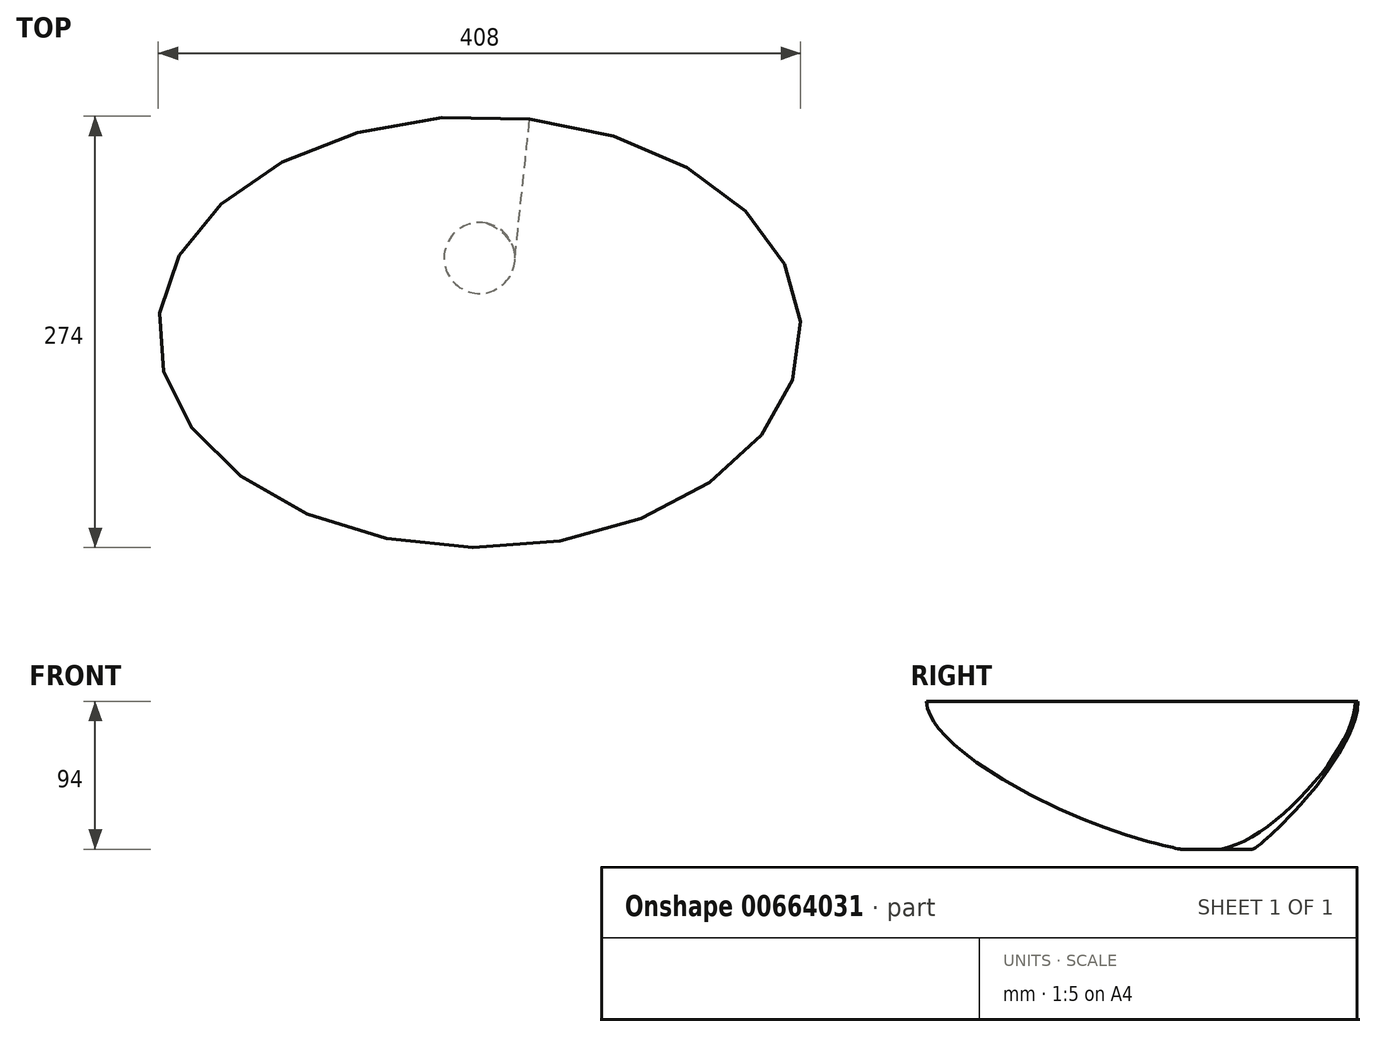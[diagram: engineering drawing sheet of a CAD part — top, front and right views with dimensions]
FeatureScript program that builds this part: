
annotation { "Feature Type Name" : "Feature", "Feature Type Description" : "" }
export const myFeature = defineFeature(function(context is Context, id is Id, definition is map)
    precondition{}
    {
        {
            var Q0;
            Q0=qCreatedBy(makeId("Top.planeOp"),FACE);
            var sketch = newSketch(context, id + "F0", { "sketchPlane" : qUnion([Q0])});
            skEllipse(sketch, "E0", {"center": v(0, 0) * mm, "majorRadius": 204 * mm, "minorRadius": 137 * mm, "majorAxis": v(1, 0)});
            skSolve(sketch);
        }
        {
            var Q0;
            Q0=makeQuery(id+"F0.imprint","IMPRINT",FACE,{"disambiguationData":[TD([[makeQuery(id+"F0.imprint","IMPRINT",EDGE,{"derivedFrom":sQuery(id+"F0.wireOp",EDGE,"E0")}),1.0]])]});
            cPlane(context, id + "F1", {"entities" : qUnion([Q0]), "cplaneType" : CPlaneType.OFFSET, "offset" : 94 * mm, "oppositeDirection" : true, "width" : 150 * mm, "height" : 150 * mm});
        }
        {
            var Q0;
            Q0=qCreatedBy(id+"F1.planeOp",FACE);
            var sketch = newSketch(context, id + "F2", { "sketchPlane" : qUnion([Q0])});
            skCircle(sketch, "E1", {"center": v(0, 47) * mm, "radius": 22.5 * mm});
            skSolve(sketch);
        }
        {
            var Q0;
            Q0=makeQuery(id+"F2.imprint","IMPRINT",FACE,{"disambiguationData":[TD([[makeQuery(id+"F2.imprint","IMPRINT",EDGE,{"derivedFrom":sQuery(id+"F2.wireOp",EDGE,"E1")}),1.0]])]});
            var Q1;
            Q1=makeQuery(id+"F0.imprint","IMPRINT",FACE,{"disambiguationData":[TD([[makeQuery(id+"F0.imprint","IMPRINT",EDGE,{"derivedFrom":sQuery(id+"F0.wireOp",EDGE,"E0")}),1.0]])]});
            loft(context, id + "F3", {"startCondition" : LoftEndDerivativeType.TANGENT_TO_PROFILE, "startMagnitude" : 1, "endCondition" : LoftEndDerivativeType.NORMAL_TO_PROFILE, "endMagnitude" : 1, "sheetProfilesArray" : [{ "sheetProfileEntities" : qUnion([Q0]) }, { "sheetProfileEntities" : qUnion([Q1]) }]});
        }
    });
